# Revit family: Table-Teknion-Zones_ZNTWD-R2015
name_source: partatom
category: Furniture
revit_build: Autodesk Revit Architecture 2015 (Build: 20140322_1515(x64)
units: mm (PartAtom-declared; Revit-internal decimal feet)

## types (3) — shared parameters
Assembly Code = E2020200
Depth = 54"
Height = 25"
Manufacturer = Teknion
Manufacturer Fax = 416.661.4586
Number of Poles = 1
Part Number = ZNTWD
Product Documentation Link = http://www.teknion.com
Product Line = Zones
Product Page URL = http://www.teknion.com
Series = Zones
Sustainability Data = http://www.teknion.com
Table Diameter = 54"
URL = http://www.teknion.com
Warranty = http://www.teknion.com
Width = 54"

## per-type parameters (varying)
| type | Description | Model | With Center Light | With Power Pill |
| Table 54", with Center Light | Round Dialogue Workshop Table, 54"dia, with Center Light Cut-Out | ZNTWD54L | Yes | No |
| Table 54'' | Round Dialogue Workshop Table, 54"dia, without Cut-Out | ZNTWD54N | No | No |
| Table 54", with Power Pill | Round Dialogue Workshop Table, 54"dia, with Center Pill Cut-Out | ZNTWD54P | No | Yes |

## geometry (parser evidence)
native form markers: Blend x146, Sweep x19
no freeform markers — native parametric forms only
